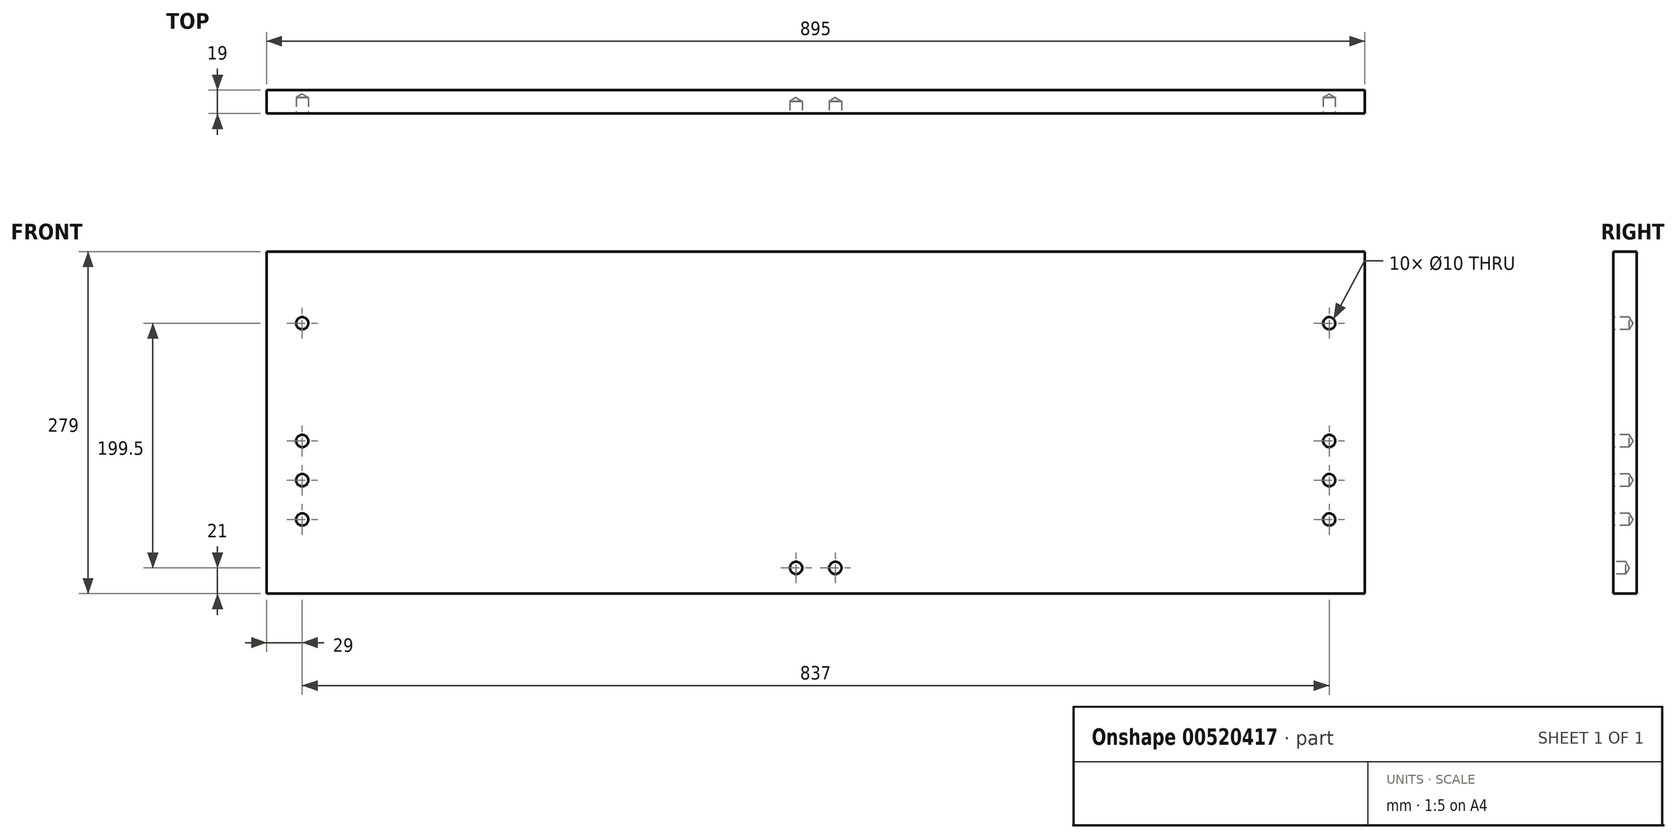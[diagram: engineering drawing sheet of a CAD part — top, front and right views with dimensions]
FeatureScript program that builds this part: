
annotation { "Feature Type Name" : "Feature", "Feature Type Description" : "" }
export const myFeature = defineFeature(function(context is Context, id is Id, definition is map)
    precondition{}
    {
        {
            var Q0;
            Q0=qCreatedBy(makeId("Right.planeOp"),FACE);
            var sketch = newSketch(context, id + "F0", { "sketchPlane" : qUnion([Q0])});
            skLineSegment(sketch, "E0.bottom", {"start": v(0, 0) * mm, "end": v(-19, 0) * mm});
            skLineSegment(sketch, "E0.top", {"start": v(0, 279) * mm, "end": v(-19, 279) * mm});
            skLineSegment(sketch, "E0.left", {"start": v(0, 0) * mm, "end": v(0, 279) * mm});
            skLineSegment(sketch, "E0.right", {"start": v(-19, 0) * mm, "end": v(-19, 279) * mm});
            skSolve(sketch);
        }
        {
            var Q0;
            Q0=makeQuery(id+"F0.imprint","IMPRINT",FACE,{"disambiguationData":[TD([[makeQuery(id+"F0.imprint","IMPRINT",EDGE,{"derivedFrom":sQuery(id+"F0.wireOp",EDGE,"E0.bottom")}),-1.0]])]});
            extrude(context, id + "F1", {"entities" : qUnion([Q0]), "depth" : 895 * mm, "offsetDistance" : 25 * mm});
        }
        {
            var Q0;
            Q0=makeQuery(id+"F1.opExtrude","SWEPT_FACE",FACE,{"disambiguationData":[OSD([sQuery(id+"F0.wireOp",EDGE,"E0.right")])]});
            var sketch = newSketch(context, id + "F2", { "sketchPlane" : qUnion([Q0])});
            skPoint(sketch, "E1", {"position": v(29, 60.5) * mm});
            skPoint(sketch, "E2", {"position": v(29, 92.5) * mm});
            skPoint(sketch, "E3", {"position": v(29, 124.5) * mm});
            skPoint(sketch, "E4", {"position": v(29, 220.5) * mm});
            skLineSegment(sketch, "E5", {"start": v(447.5, 279) * mm, "end": v(447.5, 0) * mm, "construction": true});
            skPoint(sketch, "E6.MirrorP", {"position": v(866, 220.5) * mm});
            skPoint(sketch, "E7.MirrorP", {"position": v(866, 92.5) * mm});
            skPoint(sketch, "E8.MirrorP", {"position": v(866, 124.5) * mm});
            skPoint(sketch, "E9.MirrorP", {"position": v(866, 60.5) * mm});
            skLineSegment(sketch, "E10", {"start": v(29, 220.5) * mm, "end": v(29, 60.5) * mm, "construction": true});
            skLineSegment(sketch, "E11", {"start": v(13.5, 174.23) * mm, "end": v(13.5, 60.5) * mm, "construction": true});
            skLineSegment(sketch, "E12", {"start": v(13.5, 60.5) * mm, "end": v(29, 60.5) * mm, "construction": true});
            skLineSegment(sketch, "E13", {"start": v(29, 60.5) * mm, "end": v(29, 13) * mm, "construction": true});
            skLineSegment(sketch, "E14", {"start": v(29, 13) * mm, "end": v(447.5, 13) * mm, "construction": true});
            skLineSegment(sketch, "E15", {"start": v(29, 21) * mm, "end": v(447.5, 21) * mm, "construction": true});
            skPoint(sketch, "E16", {"position": v(431.5, 21) * mm});
            skPoint(sketch, "E17.MirrorP", {"position": v(463.5, 21) * mm});
            skSolve(sketch);
        }
        {
            var Q0;
            Q0=sQuery(id+"F2.wireOp",VERTEX,"E10.start");
            var Q1;
            Q1=sQuery(id+"F2.wireOp",VERTEX,"E3");
            var Q2;
            Q2=sQuery(id+"F2.wireOp",VERTEX,"E2");
            var Q3;
            Q3=sQuery(id+"F2.wireOp",VERTEX,"E1");
            var Q4;
            Q4=sQuery(id+"F2.wireOp",VERTEX,"E9.MirrorP");
            var Q5;
            Q5=sQuery(id+"F2.wireOp",VERTEX,"E7.MirrorP");
            var Q6;
            Q6=sQuery(id+"F2.wireOp",VERTEX,"E8.MirrorP");
            var Q7;
            Q7=sQuery(id+"F2.wireOp",VERTEX,"E6.MirrorP");
            var Q8;
            Q8=makeQuery(id+"F1.opExtrude","SWEPT_BODY",BODY,{"disambiguationData":[OSD([sQuery(id+"F0.wireOp",EDGE,"E0.bottom"),sQuery(id+"F0.wireOp",EDGE,"E0.top"),sQuery(id+"F0.wireOp",EDGE,"E0.left"),sQuery(id+"F0.wireOp",EDGE,"E0.right")])]});
            hole(context, id + "F3", {"style" : HoleStyle.SIMPLE, "endStyle" : HoleEndStyle.BLIND, "holeDiameter" : 10 * mm, "majorDiameter" : 5 * mm, "holeDepth" : 13 * mm, "isTappedThrough" : true, "tappedDepth" : 12 * mm, "tapClearance" : 3, "startFromSketch" : true, "locations" : qUnion([Q0, Q1, Q2, Q3, Q4, Q5, Q6, Q7]), "scope" : qUnion([Q8])});
        }
        {
            var Q0;
            Q0=sQuery(id+"F2.wireOp",VERTEX,"E16");
            var Q1;
            Q1=sQuery(id+"F2.wireOp",VERTEX,"E17.MirrorP");
            var Q2;
            Q2=makeQuery(id+"F1.opExtrude","SWEPT_BODY",BODY,{"disambiguationData":[OSD([sQuery(id+"F0.wireOp",EDGE,"E0.bottom"),sQuery(id+"F0.wireOp",EDGE,"E0.top"),sQuery(id+"F0.wireOp",EDGE,"E0.left"),sQuery(id+"F0.wireOp",EDGE,"E0.right")])]});
            hole(context, id + "F4", {"style" : HoleStyle.SIMPLE, "endStyle" : HoleEndStyle.BLIND, "holeDiameter" : 10 * mm, "majorDiameter" : 5 * mm, "holeDepth" : 10 * mm, "isTappedThrough" : true, "tappedDepth" : 12 * mm, "tapClearance" : 3, "startFromSketch" : true, "locations" : qUnion([Q0, Q1]), "scope" : qUnion([Q2])});
        }
    });
